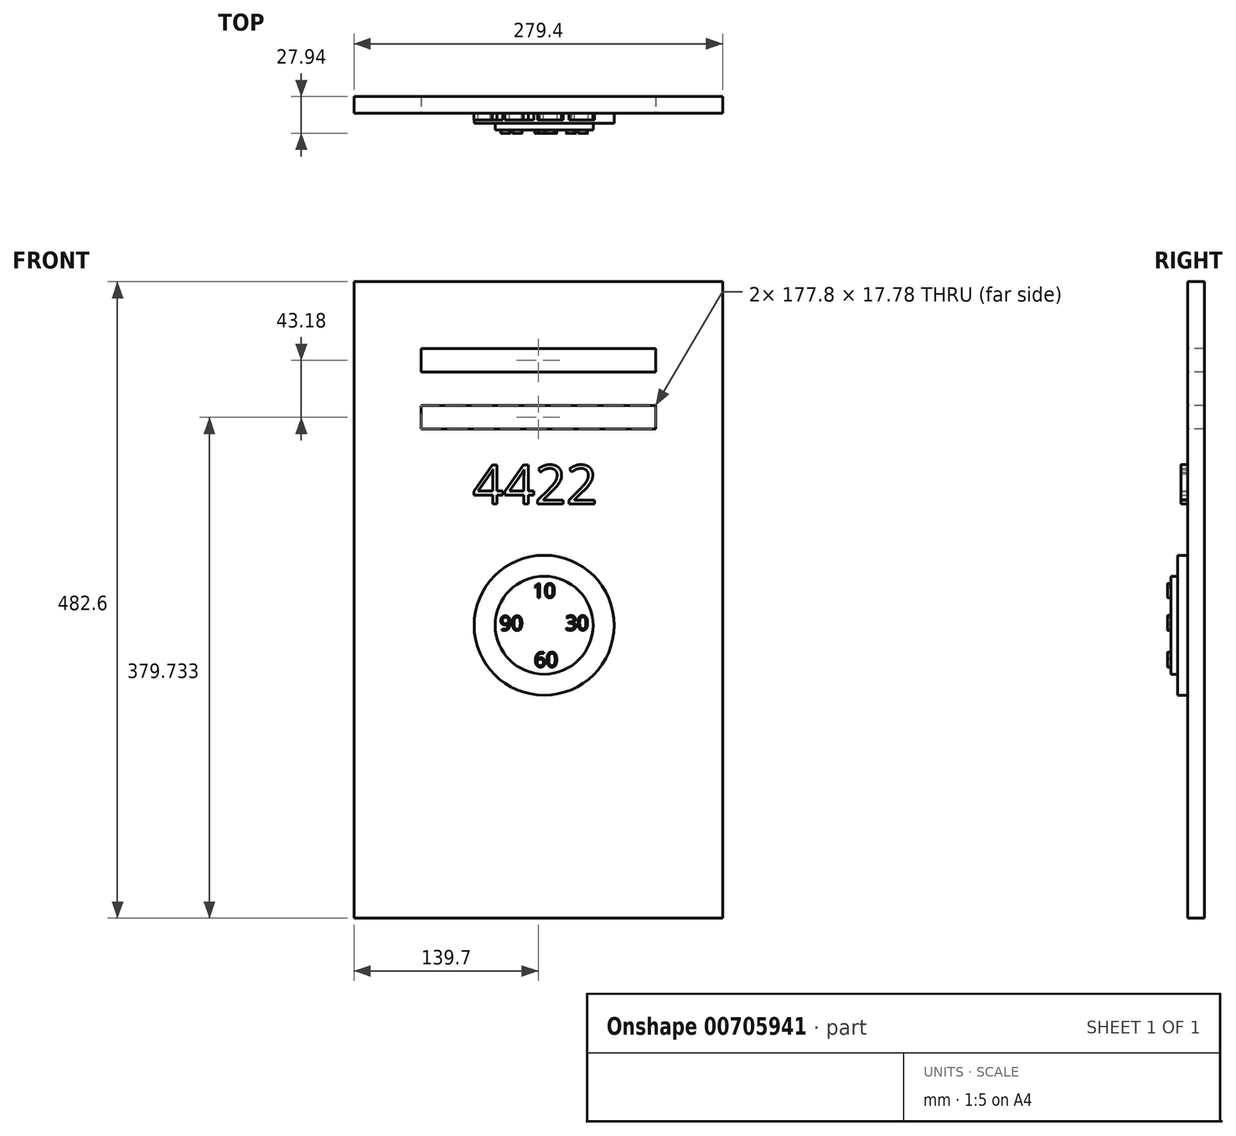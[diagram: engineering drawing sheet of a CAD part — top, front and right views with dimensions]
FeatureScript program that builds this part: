
annotation { "Feature Type Name" : "Feature", "Feature Type Description" : "" }
export const myFeature = defineFeature(function(context is Context, id is Id, definition is map)
    precondition{}
    {
        {
            var Q0;
            Q0=qCreatedBy(makeId("Front.planeOp"),FACE);
            var sketch = newSketch(context, id + "F0", { "sketchPlane" : qUnion([Q0])});
            skLineSegment(sketch, "E0.bottom", {"start": v(-144.13, 310.23) * mm, "end": v(135.27, 310.23) * mm});
            skLineSegment(sketch, "E0.top", {"start": v(-144.13, -172.37) * mm, "end": v(135.27, -172.37) * mm});
            skLineSegment(sketch, "E0.left", {"start": v(-144.13, 310.23) * mm, "end": v(-144.13, -172.37) * mm});
            skLineSegment(sketch, "E0.right", {"start": v(135.27, 310.23) * mm, "end": v(135.27, -172.37) * mm});
            skSolve(sketch);
        }
        {
            var Q0;
            Q0=makeQuery(id+"F0.imprint","IMPRINT",FACE,{"disambiguationData":[TD([[makeQuery(id+"F0.imprint","IMPRINT",EDGE,{"derivedFrom":sQuery(id+"F0.wireOp",EDGE,"E0.bottom")}),-1.0]])]});
            extrude(context, id + "F1", {"entities" : qUnion([Q0]), "depth" : 12.7 * mm, "offsetDistance" : 25.4 * mm});
        }
        {
            var Q0;
            Q0=makeQuery(id+"F1.opExtrude","CAP_FACE",FACE,{"disambiguationData":[OSD([sQuery(id+"F0.wireOp",EDGE,"E0.bottom"),sQuery(id+"F0.wireOp",EDGE,"E0.top"),sQuery(id+"F0.wireOp",EDGE,"E0.left"),sQuery(id+"F0.wireOp",EDGE,"E0.right")])],"isStart":false});
            var sketch = newSketch(context, id + "F2", { "sketchPlane" : qUnion([Q0])});
            skLineSegment(sketch, "E1.bottom", {"start": v(-93.33, 259.43) * mm, "end": v(84.47, 259.43) * mm});
            skLineSegment(sketch, "E1.top", {"start": v(-93.33, 241.65) * mm, "end": v(84.47, 241.65) * mm});
            skLineSegment(sketch, "E1.left", {"start": v(-93.33, 259.43) * mm, "end": v(-93.33, 241.65) * mm});
            skLineSegment(sketch, "E1.right", {"start": v(84.47, 259.43) * mm, "end": v(84.47, 241.65) * mm});
            skLineSegment(sketch, "E2.bottom", {"start": v(-93.33, 216.25) * mm, "end": v(84.47, 216.25) * mm});
            skLineSegment(sketch, "E2.top", {"start": v(-93.33, 198.47) * mm, "end": v(84.47, 198.47) * mm});
            skLineSegment(sketch, "E2.left", {"start": v(-93.33, 216.25) * mm, "end": v(-93.33, 198.47) * mm});
            skLineSegment(sketch, "E2.right", {"start": v(84.47, 216.25) * mm, "end": v(84.47, 198.47) * mm});
            skSolve(sketch);
        }
        {
            var Q0;
            Q0=makeQuery(id+"F2.imprint","IMPRINT",FACE,{"disambiguationData":[TD([[makeQuery(id+"F2.imprint","IMPRINT",EDGE,{"derivedFrom":sQuery(id+"F2.wireOp",EDGE,"E1.bottom")}),-1.0]])]});
            var Q1;
            Q1=makeQuery(id+"F2.imprint","IMPRINT",FACE,{"disambiguationData":[TD([[makeQuery(id+"F2.imprint","IMPRINT",EDGE,{"derivedFrom":sQuery(id+"F2.wireOp",EDGE,"E2.bottom")}),-1.0]])]});
            extrude(context, id + "F3", {"entities" : qUnion([Q0, Q1]), "operationType" : NewBodyOperationType.REMOVE, "oppositeDirection" : true, "depth" : 25.4 * mm, "offsetDistance" : 25.4 * mm});
        }
        {
            var Q0;
            Q0=makeQuery(id+"F1.opExtrude","CAP_FACE",FACE,{"disambiguationData":[OSD([sQuery(id+"F0.wireOp",EDGE,"E0.bottom"),sQuery(id+"F0.wireOp",EDGE,"E0.top"),sQuery(id+"F0.wireOp",EDGE,"E0.left"),sQuery(id+"F0.wireOp",EDGE,"E0.right")])],"isStart":false});
            var sketch = newSketch(context, id + "F4", { "sketchPlane" : qUnion([Q0])});
            skText(sketch, "E3", { "text": "4422\n", "fontName": "OpenSans-Regular.ttf"});
            const initialGuessF4  = {"E3": [-0.05417, 0.14163, 1, 0, 0.02976]};
            skSetInitialGuess(sketch, initialGuessF4);
            skSolve(sketch);
        }
        {
            var Q0;
            Q0 = qSketchRegion(id + "F4", true);
            extrude(context, id + "F5", {"entities" : qUnion([Q0]), "operationType" : NewBodyOperationType.ADD, "depth" : 5.08 * mm, "offsetDistance" : 25.4 * mm});
        }
        {
            var Q0;
            {var subQ0=sQuery(id+"F0.wireOp",EDGE,"E0.bottom");var subQ1=sQuery(id+"F0.wireOp",EDGE,"E0.right");var subQ2=sQuery(id+"F0.wireOp",EDGE,"E0.top");var subQ3=sQuery(id+"F0.wireOp",EDGE,"E0.left");Q0=makeQuery(id+"F5.boolean.opBoolean","SPLIT",FACE,{"disambiguationData":[TD([makeQuery(id+"F1.opExtrude","SWEPT_FACE",FACE,{"disambiguationData":[OSD([subQ0])]})])],"derivedFrom":makeQuery(id+"F1.opExtrude","CAP_FACE",FACE,{"disambiguationData":[OSD([subQ0,subQ2,subQ3,subQ1])],"isStart":false})});}
            var sketch = newSketch(context, id + "F6", { "sketchPlane" : qUnion([Q0])});
            skCircle(sketch, "E4", {"center": v(0, 49.8) * mm, "radius": 53.04 * mm});
            skSolve(sketch);
        }
        {
            var Q0;
            Q0 = qSketchRegion(id + "F6", true);
            extrude(context, id + "F7", {"entities" : qUnion([Q0]), "operationType" : NewBodyOperationType.ADD, "depth" : 7.62 * mm, "offsetDistance" : 25.4 * mm});
        }
        {
            var Q0;
            {var subQ0=sQuery(id+"F0.wireOp",EDGE,"E0.bottom");var subQ1=sQuery(id+"F0.wireOp",EDGE,"E0.right");var subQ2=sQuery(id+"F0.wireOp",EDGE,"E0.top");var subQ3=sQuery(id+"F0.wireOp",EDGE,"E0.left");Q0=makeQuery(id+"F5.boolean.opBoolean","SPLIT",FACE,{"disambiguationData":[TD([makeQuery(id+"F1.opExtrude","SWEPT_FACE",FACE,{"disambiguationData":[OSD([subQ0])]})])],"derivedFrom":makeQuery(id+"F1.opExtrude","CAP_FACE",FACE,{"disambiguationData":[OSD([subQ0,subQ2,subQ3,subQ1])],"isStart":false})});}
            var sketch = newSketch(context, id + "F8", { "sketchPlane" : qUnion([Q0])});
            skCircle(sketch, "E5", {"center": v(0, 49.8) * mm, "radius": 37.12 * mm});
            skSolve(sketch);
        }
        {
            var Q0;
            Q0 = qSketchRegion(id + "F8", true);
            extrude(context, id + "F9", {"entities" : qUnion([Q0]), "operationType" : NewBodyOperationType.ADD, "depth" : 12.7 * mm, "offsetDistance" : 25.4 * mm});
        }
        {
            var Q0;
            Q0=makeQuery(id+"F9.opExtrude","CAP_FACE",FACE,{"disambiguationData":[OSD([sQuery(id+"F8.wireOp",EDGE,"E5")])],"isStart":false});
            var sketch = newSketch(context, id + "F10", { "sketchPlane" : qUnion([Q0])});
            skText(sketch, "E6", { "text": "60", "fontName": "OpenSans-Regular.ttf"});
            skText(sketch, "E7", { "text": "90", "fontName": "OpenSans-Regular.ttf"});
            skText(sketch, "E8", { "text": "30", "fontName": "OpenSans-Regular.ttf"});
            skText(sketch, "E9", { "text": "10", "fontName": "OpenSans-Regular.ttf"});
            const initialGuessF10  = {"E6": [-0.0075, 0.0182, 1, 0, 0.01123], "E7": [-0.03363, 0.04588, 1, 0, 0.01104], "E8": [0.01613, 0.04607, 1, 0, 0.01104], "E9": [-0.00866, 0.07066, 1, 0, 0.01084]};
            skSetInitialGuess(sketch, initialGuessF10);
            skSolve(sketch);
        }
        {
            var Q0;
            Q0 = qSketchRegion(id + "F10", true);
            extrude(context, id + "F11", {"entities" : qUnion([Q0]), "operationType" : NewBodyOperationType.ADD, "depth" : 2.54 * mm, "offsetDistance" : 25.4 * mm});
        }
    });
